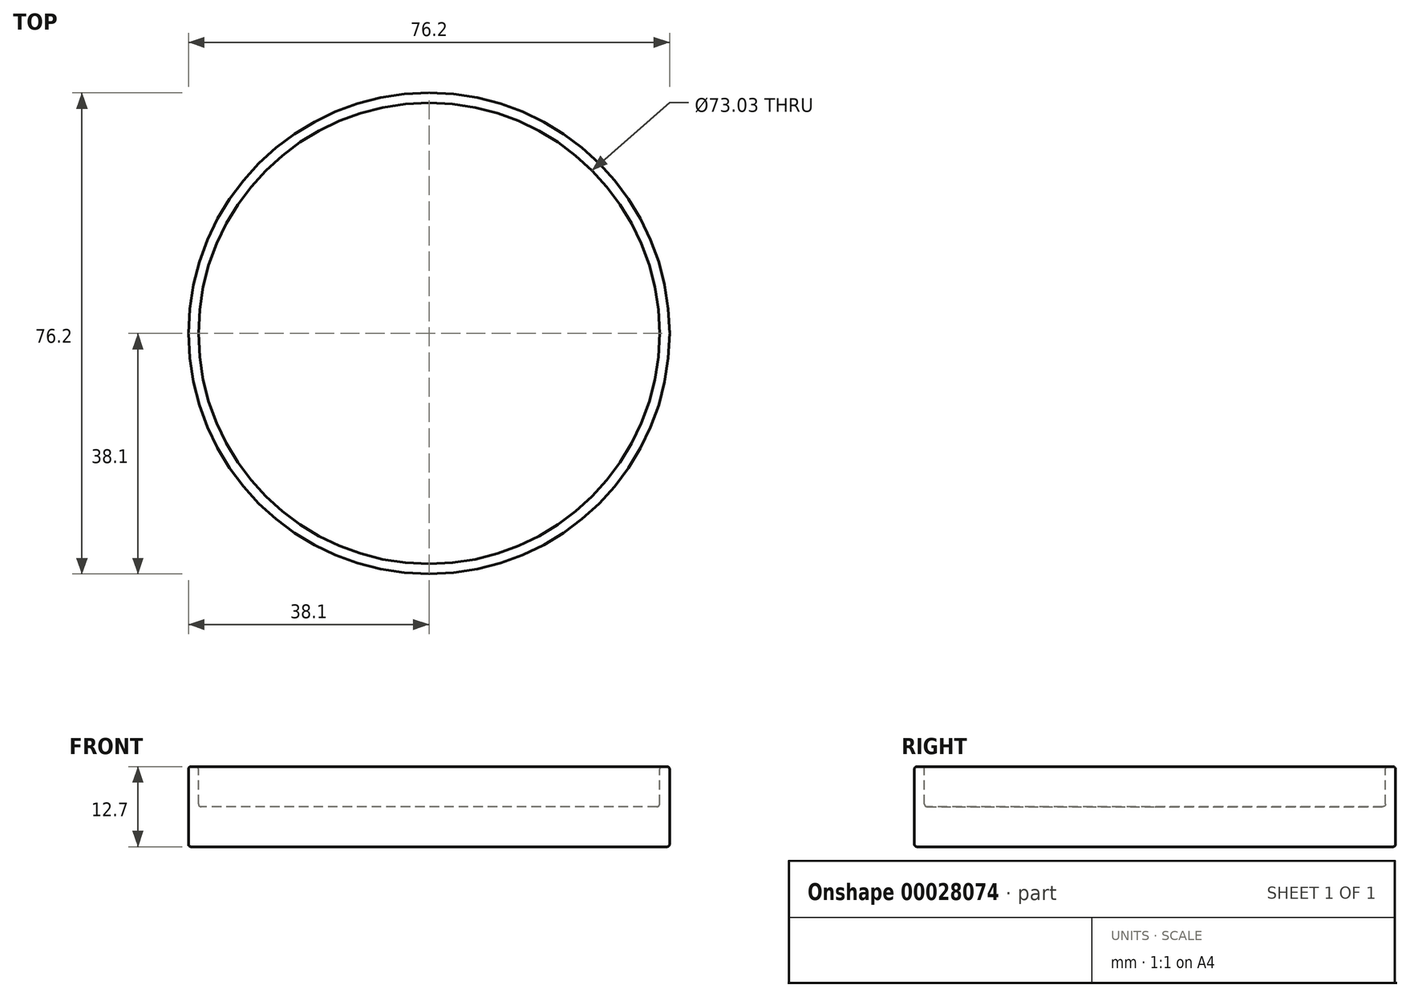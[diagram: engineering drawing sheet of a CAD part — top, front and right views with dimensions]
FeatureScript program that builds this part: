
annotation { "Feature Type Name" : "Feature", "Feature Type Description" : "" }
export const myFeature = defineFeature(function(context is Context, id is Id, definition is map)
    precondition{}
    {
        {
            var Q0;
            Q0=qCreatedBy(makeId("Front.planeOp"),FACE);
            var sketch = newSketch(context, id + "F0", { "sketchPlane" : qUnion([Q0])});
            skLineSegment(sketch, "E0", {"start": v(0, 21.94) * mm, "end": v(0, -28.5) * mm, "construction": true});
            skLineSegment(sketch, "E1", {"start": v(0, 0) * mm, "end": v(37.7, 0) * mm});
            skLineSegment(sketch, "E2", {"start": v(38.1, 0.4) * mm, "end": v(38.1, 12.3) * mm});
            skLineSegment(sketch, "E3", {"start": v(37.7, 12.7) * mm, "end": v(36.9, 12.7) * mm});
            skLineSegment(sketch, "E4", {"start": v(36.51, 12.3) * mm, "end": v(36.51, 6.75) * mm});
            skLineSegment(sketch, "E5", {"start": v(36.12, 6.35) * mm, "end": v(0, 6.35) * mm});
            skLineSegment(sketch, "E6", {"start": v(0, 6.35) * mm, "end": v(0, 0) * mm});
            skPoint(sketch, "E7.visualSharp", {"position": v(36.51, 6.35) * mm});
            skArc(sketch, "E7.filletArc", {"start": v(36.12, 6.35) * mm, "mid": v(36.4, 6.47) * mm, "end": v(36.51, 6.75) * mm});
            skPoint(sketch, "E8.visualSharp", {"position": v(36.51, 12.7) * mm});
            skArc(sketch, "E8.filletArc", {"start": v(36.9, 12.7) * mm, "mid": v(36.63, 12.58) * mm, "end": v(36.51, 12.3) * mm});
            skPoint(sketch, "E9.visualSharp", {"position": v(38.1, 12.7) * mm});
            skArc(sketch, "E9.filletArc", {"start": v(38.1, 12.3) * mm, "mid": v(37.98, 12.58) * mm, "end": v(37.7, 12.7) * mm});
            skPoint(sketch, "E10.visualSharp", {"position": v(38.1, 0) * mm});
            skArc(sketch, "E10.filletArc", {"start": v(37.7, 0) * mm, "mid": v(37.98, 0.12) * mm, "end": v(38.1, 0.4) * mm});
            skSolve(sketch);
        }
        {
            var Q0;
            Q0=makeQuery(id+"F0.imprint","IMPRINT",FACE,{"disambiguationData":[TD([[makeQuery(id+"F0.imprint","IMPRINT",EDGE,{"derivedFrom":sQuery(id+"F0.wireOp",EDGE,"E1")}),1.0]])]});
            var Q1;
            Q1=sQuery(id+"F0.wireOp",EDGE,"E0");
            revolve(context, id + "F1", {"entities" : qUnion([Q0]), "axis" : qUnion([Q1]), "revolveType" : RevolveType.FULL});
        }
    });
